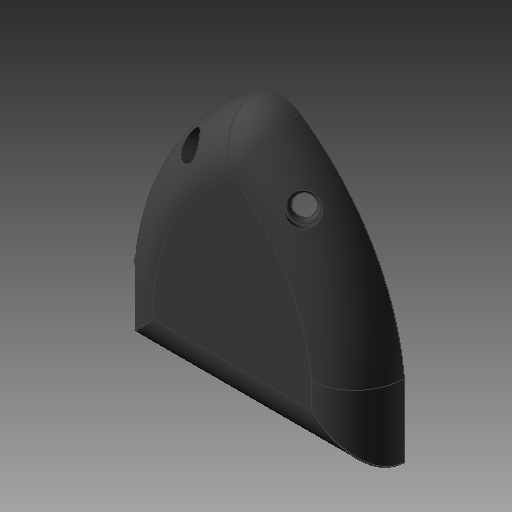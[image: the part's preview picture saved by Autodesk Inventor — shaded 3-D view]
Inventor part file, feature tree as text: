
AUTODESK INVENTOR PART (.ipt)
format: ipt  version: 2018 (Build 220112000, 112)  size: 421,888 bytes
history: native  units: mm
features: sketch x11, reference x11, extrude x9, other x8, fillet x7, plane x4, projected_geometry x1
ambient origin geometry x8: Origin, YZ Plane, XZ Plane, XY Plane, X Axis, Y Axis, Z Axis, Center Point
bodies: Solid1 (feature_tree)
feature tree (51):
  extrude  "Extrusion1"  Depth=40.0mm
  sketch  "Sketch3"  dims[d14=15.0mm d15=15.0mm]
  other  "Work Point7"
  other  "Work Point8"
  plane  "Work Plane3"
  plane  "Work Plane4"
  sketch  "Sketch4"  dims[d16=10.0mm d17=0.0mm d18=10.0mm d19=0.0mm d20=25.0mm]
  plane  "Work Plane5"
  plane  "Work Plane6"
  sketch  "Sketch7"  dims[d21=10.0mm d22=10.0mm]
  extrude  "Extrusion4"  Depth=15.0mm
  extrude  "Extrusion5"  Depth=10.0mm TaperAngle=0.0deg
  fillet  "Fillet3"  Radius=25.0mm
  sketch  "Sketch9"  dims[d27=12.5mm d28=0.0mm d29=2.0mm d30=2.0mm d31=10.0mm d32=0.0mm]
  sketch  "Sketch10"  dims[d33=13.0mm d34=10.0mm d35=0.0mm]
  extrude  "Extrusion6"  Depth=10.0mm
  extrude  "Extrusion7"  Depth=30.0mm TaperAngle=0.0deg
  extrude  "Extrusion8"  Depth=2.0mm
  fillet  "Fillet4"  Radius=2.0mm
  fillet  "Fillet5"  Radius=10.0mm
  extrude  "Extrusion9"  Depth=10.0mm TaperAngle=0.0deg
  extrude  "Extrusion10"  Depth=10.0mm
  fillet  "Fillet6"  Radius=8.0mm
  extrude  "Extrusion11"  Depth=1.0mm
  fillet  "Fillet7"  Radius=2.0mm
  fillet  "Fillet8"  [1 undecoded]
  fillet  "Fillet9"  [1 undecoded]
  sketch  "Sketch1"  dims[d0=25.0mm d1=0.0mm d4=40.0mm]
  reference  "Reference1"
  sketch  "Sketch8"  dims[d23=30.0mm d24=0.0mm d25=30.0mm d26=0.0mm]
  sketch  "Sketch11"  dims[d36=2.0mm d37=10.0mm d38=8.0mm d39=0.0mm]
  reference  "Reference2"
  reference  "Reference3"
  reference  "Reference4"
  reference  "Reference5"
  reference  "Reference6"
  reference  "Reference7"
  reference  "Reference8"
  reference  "Reference9"
  reference  "Reference10"
  reference  "Reference12"
  sketch  "Sketch12"  dims[d40=1.0mm d41=1.0mm d42=2.0mm]
  projected_geometry  "Projected Loop1"
  sketch  "Sketch13"
  sketch  "Sketch14"
  other  "<userpath>\OneDrive\Documents\Inventor\TSA\2018\Animatronics\Tortoise\Head\HeadAssembly.iam"
  other  "HeadAssembly.iam"
  other  "HeadTop:1"
  other  "<userpath>\OneDrive\Documents\Inventor\TSA\2018\Animatronics\Tortoise\TurtleAssembly2.iam"
  other  "TurtleAssembly2.iam"
  other  "HeadBottom:1"
note: 2 required parameter values undecoded (feature->parameter linkage not recoverable at this tier; creation-order binding heuristic only, values carry confidence <= 0.55)
